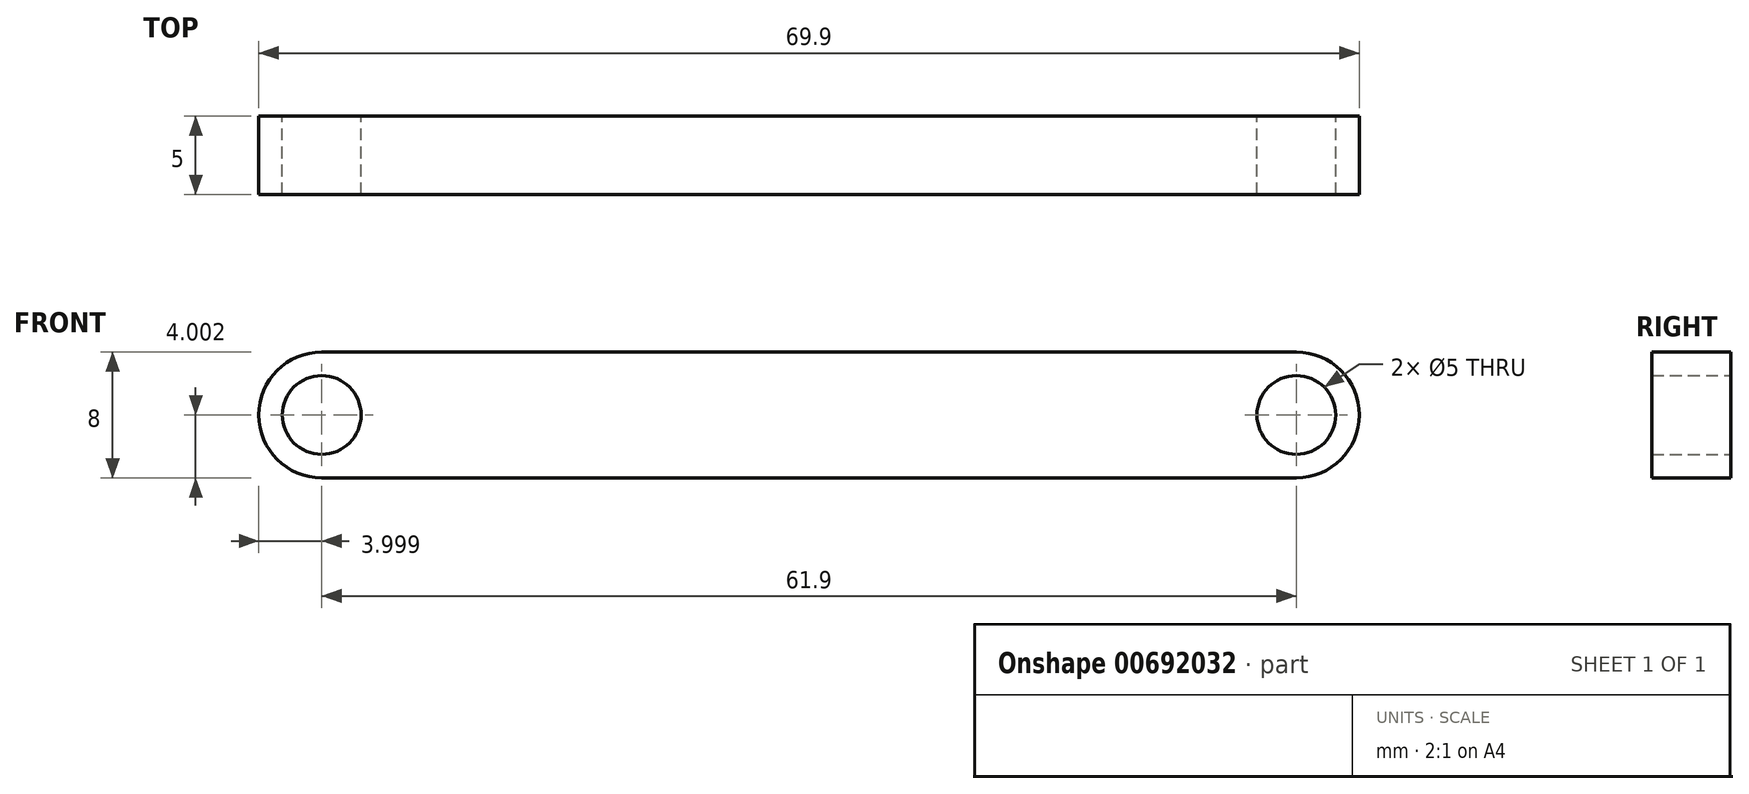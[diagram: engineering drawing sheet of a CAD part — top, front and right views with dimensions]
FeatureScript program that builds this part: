
annotation { "Feature Type Name" : "Feature", "Feature Type Description" : "" }
export const myFeature = defineFeature(function(context is Context, id is Id, definition is map)
    precondition{}
    {
        {
            var Q0;
            Q0=qCreatedBy(makeId("Front.planeOp"),FACE);
            var sketch = newSketch(context, id + "F0", { "sketchPlane" : qUnion([Q0])});
            skLineSegment(sketch, "E0.bottom", {"start": v(-31.81, 3.98) * mm, "end": v(30.09, 3.98) * mm});
            skLineSegment(sketch, "E0.top", {"start": v(-31.81, -4.02) * mm, "end": v(30.09, -4.02) * mm});
            skArc(sketch, "E1", {"start": v(-31.81, 3.98) * mm, "mid": v(-35.81, -0.02) * mm, "end": v(-31.81, -4.02) * mm});
            skArc(sketch, "E2", {"start": v(30.09, -4.02) * mm, "mid": v(34.09, -0.02) * mm, "end": v(30.09, 3.98) * mm});
            skCircle(sketch, "E3", {"center": v(-31.81, -0.02) * mm, "radius": 2.5 * mm});
            skCircle(sketch, "E4", {"center": v(30.09, -0.02) * mm, "radius": 2.5 * mm});
            skSolve(sketch);
        }
        {
            var Q0;
            Q0=makeQuery(id+"F0.imprint","IMPRINT",FACE,{"disambiguationData":[TD([[makeQuery(id+"F0.imprint","IMPRINT",EDGE,{"derivedFrom":sQuery(id+"F0.wireOp",EDGE,"E0.bottom")}),-1.0]])]});
            extrude(context, id + "F1", {"entities" : qUnion([Q0]), "depth" : 5 * mm, "offsetDistance" : 25 * mm});
        }
    });
